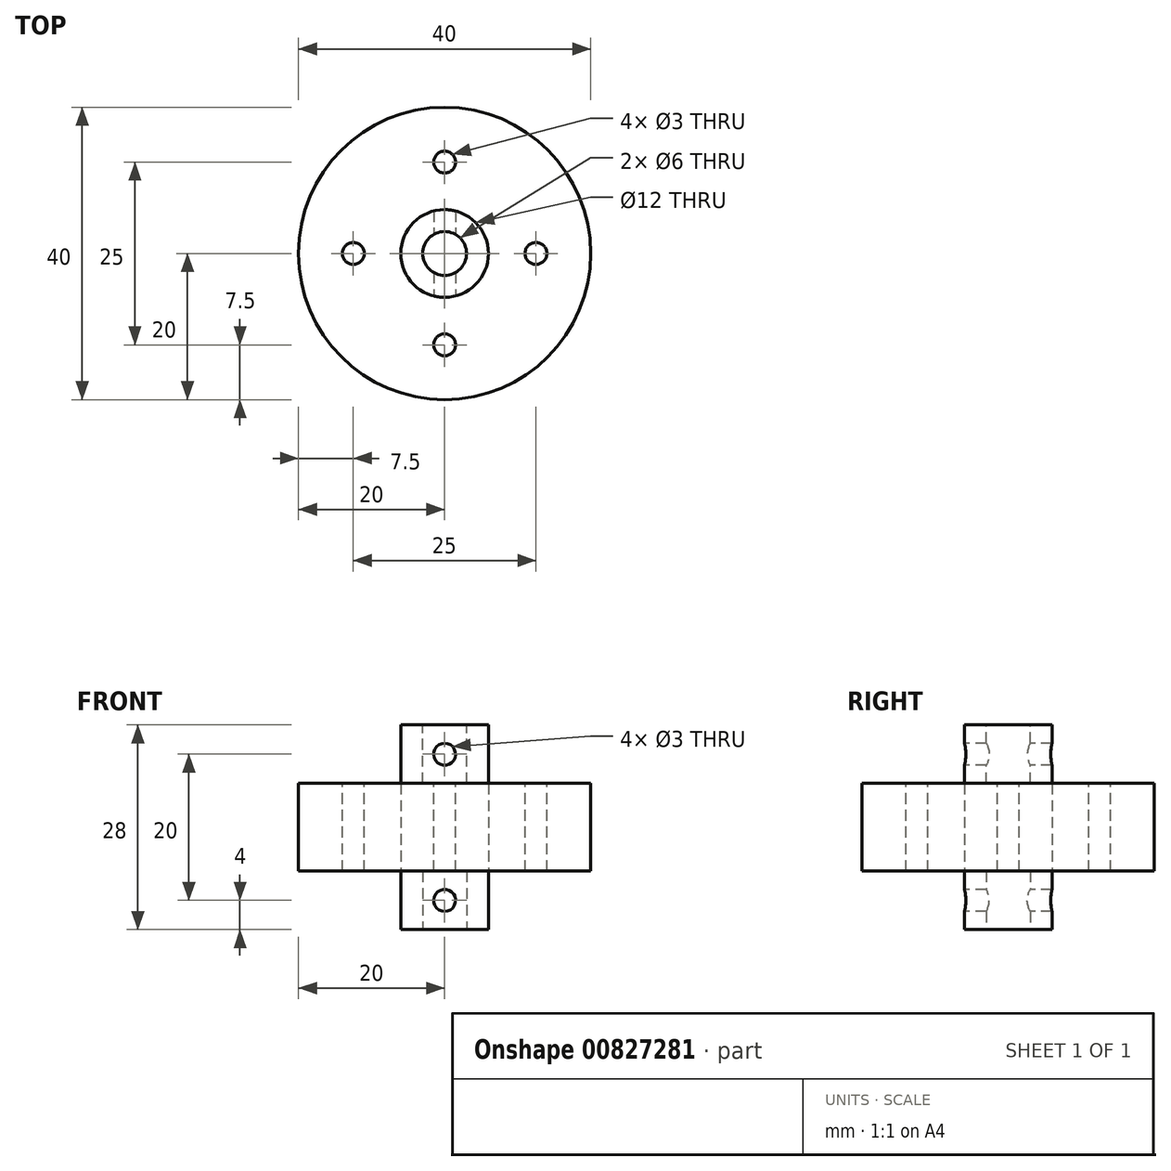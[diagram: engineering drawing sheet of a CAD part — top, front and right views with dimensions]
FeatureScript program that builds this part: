
annotation { "Feature Type Name" : "Feature", "Feature Type Description" : "" }
export const myFeature = defineFeature(function(context is Context, id is Id, definition is map)
    precondition{}
    {
        {
            var Q0;
            Q0=qCreatedBy(makeId("Top.planeOp"),FACE);
            var sketch = newSketch(context, id + "F0", { "sketchPlane" : qUnion([Q0])});
            skCircle(sketch, "E0", {"center": v(0, 0) * mm, "radius": 6 * mm});
            skCircle(sketch, "E1", {"center": v(0, 0) * mm, "radius": 3 * mm});
            skSolve(sketch);
        }
        {
            var Q0;
            Q0=makeQuery(id+"F0.imprint","IMPRINT",FACE,{"disambiguationData":[TD([[makeQuery(id+"F0.imprint","IMPRINT",EDGE,{"derivedFrom":sQuery(id+"F0.wireOp",EDGE,"E0")}),1.0]])]});
            extrude(context, id + "F1", {"entities" : qUnion([Q0]), "depth" : 8 * mm, "offsetDistance" : 25 * mm});
        }
        {
            var Q0;
            Q0=makeQuery(id+"F1.opExtrude","CAP_FACE",FACE,{"disambiguationData":[OSD([sQuery(id+"F0.wireOp",EDGE,"E0"),sQuery(id+"F0.wireOp",EDGE,"E1")])],"isStart":false});
            var sketch = newSketch(context, id + "F2", { "sketchPlane" : qUnion([Q0])});
            skCircle(sketch, "E2", {"center": v(0, 0) * mm, "radius": 20 * mm});
            skSolve(sketch);
        }
        {
            var Q0;
            Q0=makeQuery(id+"F2.imprint","IMPRINT",FACE,{"disambiguationData":[TD([[makeQuery(id+"F2.imprint","IMPRINT",EDGE,{"derivedFrom":sQuery(id+"F2.wireOp",EDGE,"E2")}),1.0]])]});
            extrude(context, id + "F3", {"entities" : qUnion([Q0]), "depth" : 6 * mm, "offsetDistance" : 25 * mm});
        }
        {
            var Q0;
            Q0=qCreatedBy(makeId("Front.planeOp"),FACE);
            var sketch = newSketch(context, id + "F4", { "sketchPlane" : qUnion([Q0])});
            skCircle(sketch, "E3", {"center": v(0, 4) * mm, "radius": 1.5 * mm});
            skSolve(sketch);
        }
        {
            var Q0;
            Q0 = qSketchRegion(id + "F4", true);
            extrude(context, id + "F5", {"entities" : qUnion([Q0]), "operationType" : NewBodyOperationType.REMOVE, "endBound" : BoundingType.THROUGH_ALL, "oppositeDirection" : true, "depth" : 25 * mm, "offsetDistance" : 25 * mm, "hasSecondDirection" : true, "secondDirectionBound" : SecondDirectionBoundingType.THROUGH_ALL, "secondDirectionOppositeDirection" : false, "secondDirectionDepth" : 25 * mm});
        }
        {
            var Q0;
            Q0=makeQuery(id+"F3.opExtrude","CAP_FACE",FACE,{"disambiguationData":[OSD([sQuery(id+"F0.wireOp",EDGE,"E0"),sQuery(id+"F2.wireOp",EDGE,"E2")])],"isStart":false});
            var sketch = newSketch(context, id + "F6", { "sketchPlane" : qUnion([Q0])});
            skCircle(sketch, "E4", {"center": v(0, 0) * mm, "radius": 12.5 * mm, "construction": true});
            skCircle(sketch, "E5", {"center": v(0, 12.5) * mm, "radius": 1.5 * mm});
            skCircle(sketch, "E6.MirrorC", {"center": v(0, -12.5) * mm, "radius": 1.5 * mm});
            skCircle(sketch, "E7", {"center": v(-12.5, 0) * mm, "radius": 1.5 * mm});
            skCircle(sketch, "E8.MirrorC", {"center": v(12.5, 0) * mm, "radius": 1.5 * mm});
            skSolve(sketch);
        }
        {
            var Q0;
            Q0 = qSketchRegion(id + "F6", true);
            extrude(context, id + "F7", {"entities" : qUnion([Q0]), "operationType" : NewBodyOperationType.REMOVE, "endBound" : BoundingType.THROUGH_ALL, "oppositeDirection" : true, "depth" : 25 * mm, "offsetDistance" : 25 * mm});
        }
        {
            var Q0;
            Q0=makeQuery(id+"F3.opExtrude","SWEPT_BODY",BODY,{"disambiguationData":[OSD([sQuery(id+"F0.wireOp",EDGE,"E0"),sQuery(id+"F2.wireOp",EDGE,"E2")])]});
            var Q1;
            Q1=makeQuery(id+"F1.opExtrude","SWEPT_BODY",BODY,{"disambiguationData":[OSD([sQuery(id+"F0.wireOp",EDGE,"E0"),sQuery(id+"F0.wireOp",EDGE,"E1")])]});
            var Q2;
            Q2=makeQuery(id+"F3.opExtrude","CAP_FACE",FACE,{"disambiguationData":[OSD([sQuery(id+"F0.wireOp",EDGE,"E0"),sQuery(id+"F2.wireOp",EDGE,"E2")])],"isStart":false});
            mirror(context, id + "F8", {"operationType" : NewBodyOperationType.ADD, "entities" : qUnion([Q0, Q1]), "mirrorPlane" : qUnion([Q2])});
        }
    });
